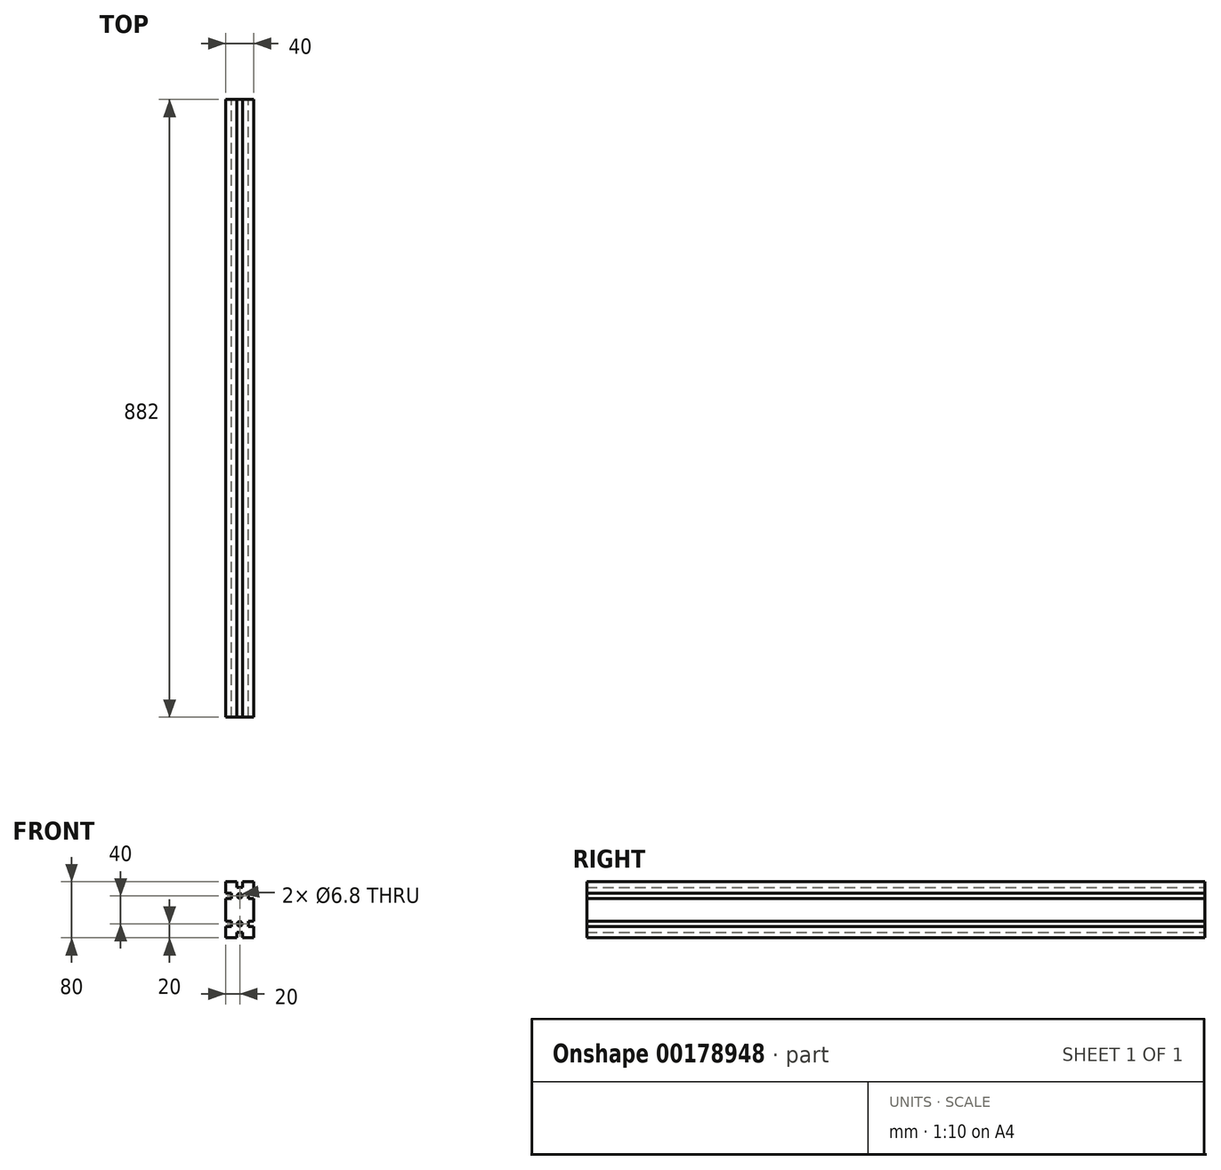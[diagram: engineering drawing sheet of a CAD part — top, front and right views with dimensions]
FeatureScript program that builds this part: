
annotation { "Feature Type Name" : "Feature", "Feature Type Description" : "" }
export const myFeature = defineFeature(function(context is Context, id is Id, definition is map)
    precondition{}
    {
        {
            var Q0;
            Q0=qCreatedBy(makeId("Front.planeOp"),FACE);
            var sketch = newSketch(context, id + "F0", { "sketchPlane" : qUnion([Q0])});
            skLineSegment(sketch, "E0.bottom", {"start": v(20, 40) * mm, "end": v(4, 40) * mm});
            skLineSegment(sketch, "E0.top", {"start": v(20, -40) * mm, "end": v(4, -40) * mm});
            skLineSegment(sketch, "E0.left", {"start": v(20, 40) * mm, "end": v(20, 23.95) * mm});
            skLineSegment(sketch, "E0.right", {"start": v(-20, 40) * mm, "end": v(-20, 24) * mm});
            skPoint(sketch, "E0.middle", {"position": v(0, 0) * mm});
            skCircle(sketch, "E1", {"center": v(0, 20) * mm, "radius": 3.4 * mm});
            skCircle(sketch, "E2", {"center": v(0, -20) * mm, "radius": 3.4 * mm});
            skLineSegment(sketch, "E3.bottom", {"start": v(-12, 16) * mm, "end": v(-20, 16) * mm});
            skLineSegment(sketch, "E3.top", {"start": v(-12, 24) * mm, "end": v(-20, 24) * mm});
            skLineSegment(sketch, "E3.left", {"start": v(-12, 16) * mm, "end": v(-12, 24) * mm});
            skPoint(sketch, "E3.middle", {"position": v(-20, 20) * mm});
            skLineSegment(sketch, "E4.bottom", {"start": v(20, 15.95) * mm, "end": v(12.06, 15.95) * mm});
            skLineSegment(sketch, "E4.top", {"start": v(20, 23.95) * mm, "end": v(12.06, 23.95) * mm});
            skLineSegment(sketch, "E4.right", {"start": v(12.06, 15.95) * mm, "end": v(12.06, 23.95) * mm});
            skLineSegment(sketch, "E5.bottom", {"start": v(-11.99, -24.06) * mm, "end": v(-20, -24.06) * mm});
            skLineSegment(sketch, "E5.top", {"start": v(-11.99, -16.06) * mm, "end": v(-20, -16.06) * mm});
            skLineSegment(sketch, "E5.left", {"start": v(-11.99, -24.06) * mm, "end": v(-11.99, -16.06) * mm});
            skLineSegment(sketch, "E6.bottom", {"start": v(20, -24.14) * mm, "end": v(12.08, -24.14) * mm});
            skLineSegment(sketch, "E6.top", {"start": v(20, -16.14) * mm, "end": v(12.08, -16.14) * mm});
            skLineSegment(sketch, "E6.right", {"start": v(12.08, -24.14) * mm, "end": v(12.08, -16.14) * mm});
            skLineSegment(sketch, "E7.trimOffspring", {"start": v(-20, -24.06) * mm, "end": v(-20, -40) * mm});
            skLineSegment(sketch, "E8.trimOffspring", {"start": v(20, -24.14) * mm, "end": v(20, -40) * mm});
            skLineSegment(sketch, "E9.trimOffspring", {"start": v(20, 15.95) * mm, "end": v(20, -16.14) * mm});
            skLineSegment(sketch, "E10.trimOffspring", {"start": v(-20, 16) * mm, "end": v(-20, -16.06) * mm});
            skPoint(sketch, "E3.right.end.orphan", {"position": v(-28, 24) * mm});
            skPoint(sketch, "E3.right.start.orphan", {"position": v(-28, 16) * mm});
            skLineSegment(sketch, "E11.bottom", {"start": v(4, 32) * mm, "end": v(-4, 32) * mm});
            skLineSegment(sketch, "E11.left", {"start": v(4, 32) * mm, "end": v(4, 40) * mm});
            skLineSegment(sketch, "E11.right", {"start": v(-4, 32) * mm, "end": v(-4, 40) * mm});
            skPoint(sketch, "E11.middle", {"position": v(0, 40) * mm});
            skLineSegment(sketch, "E12.top", {"start": v(4, -32) * mm, "end": v(-4, -32) * mm});
            skLineSegment(sketch, "E12.left", {"start": v(4, -40) * mm, "end": v(4, -32) * mm});
            skLineSegment(sketch, "E12.right", {"start": v(-4, -40) * mm, "end": v(-4, -32) * mm});
            skPoint(sketch, "E12.middle", {"position": v(0, -40) * mm});
            skPoint(sketch, "E13.orphan", {"position": v(-4, 48) * mm});
            skLineSegment(sketch, "E14.trimOffspring", {"start": v(-4, 40) * mm, "end": v(-20, 40) * mm});
            skPoint(sketch, "E15.orphan", {"position": v(4, 48) * mm});
            skPoint(sketch, "E16.orphan", {"position": v(4, -48) * mm});
            skLineSegment(sketch, "E17.trimOffspring", {"start": v(-4, -40) * mm, "end": v(-20, -40) * mm});
            skPoint(sketch, "E18.orphan", {"position": v(-4, -48) * mm});
            skSolve(sketch);
        }
        {
            var Q0;
            Q0=makeQuery(id+"F0.imprint","IMPRINT",FACE,{"disambiguationData":[TD([[makeQuery(id+"F0.imprint","IMPRINT",EDGE,{"derivedFrom":sQuery(id+"F0.wireOp",EDGE,"E0.bottom")}),1.0]])]});
            extrude(context, id + "F1", {"entities" : qUnion([Q0]), "depth" : 882 * mm});
        }
    });
